# Revit family: okamura_CDC7BE-CDC7BF-CDC7BL-CDC7BM_Cynara_Black Body Fixed Armrest Normal Caster_1
name_source: partatom
category: Furniture
revit_build: Autodesk Revit 2017 (Build: 20160225_1515(x64)
units: mm (PartAtom-declared; Revit-internal decimal feet)

## family parameters
Always vertical = Yes
Cut with Voids When Loaded = No
OmniClass Number = 23.40.20.00
OmniClass Title = General Furniture and Specialties
Room Calculation Point = No
Shared = No
Work Plane-Based = No

## types (24) — shared parameters
Assembly Code = E2020200
Body & Base = okm_G721
Caster = okm_G155
D = 505 mm
Gas Lift = okm_silver FX4
H = 999 mm
Keynote = 12490
Kind = Chair
Manufacturer = Okamura Corporation
Other = okm_G155
Product Categories = Office Seating
URL = http://www.okamura.co.jp
W = 626 mm

## per-type parameters (varying)
| type | Mesh | Product Number |
| F2X1(Black)_Without Brake Hard Caster | okm_F2X1 | CDC7BE |
| F2X2(White)_Without Brake Soft Caster | okm_F2X2 | CDC7BL |
| F2X3(Dark Gray)_With Brake Soft Caster | okm_F2X3 | CDC7BM |
| F2X4(Sage)_With Brake Soft Caster | okm_F2X4 | CDC7BM |
| F2X5(Dark Green)_Without Brake Soft Caster | okm_F2X5 | CDC7BL |
| F2X6(Orange Red)_With Brake Soft Caster | okm_F2X6 | CDC7BM |
| F2X1(Black)_Without Brake Soft Caster | okm_F2X1 | CDC7BL |
| F2X1(Black)_With Brake Soft Caster | okm_F2X1 | CDC7BM |
| F2X1(Black)_With Brake Hard Caster | okm_F2X1 | CDC7BF |
| F2X2(White)_Without Brake Hard Caster | okm_F2X2 | CDC7BE |
| F2X2(White)_With Brake Hard Caster | okm_F2X2 | CDC7BF |
| F2X2(White)_With Brake Soft Caster | okm_F2X2 | CDC7BM |
| F2X3(Dark Gray)_With Brake Hard Caster | okm_F2X3 | CDC7BF |
| F2X3(Dark Gray)_Without Brake Hard Caster | okm_F2X3 | CDC7BE |
| F2X3(Dark Gray)_Without Brake Soft Caster | okm_F2X3 | CDC7BL |
| F2X4(Sage)_With Brake Hard Caster | okm_F2X4 | CDC7BF |
| F2X4(Sage)_Without Brake Hard Caster | okm_F2X4 | CDC7BE |
| F2X4(Sage)_Without Brake Soft Caster | okm_F2X4 | CDC7BL |
| F2X5(Dark Green)_Without Brake Hard Caster | okm_F2X5 | CDC7BE |
| F2X5(Dark Green)_With Brake Hard Caster | okm_F2X5 | CDC7BF |
| F2X5(Dark Green)_With Brake Soft Caster | okm_F2X5 | CDC7BM |
| F2X6(Orange Red)_With Brake Hard Caster | okm_F2X6 | CDC7BF |
| F2X6(Orange Red)_Without Brake Hard Caster | okm_F2X6 | CDC7BE |
| F2X6(Orange Red)_Without Brake Soft Caster | okm_F2X6 | CDC7BL |
